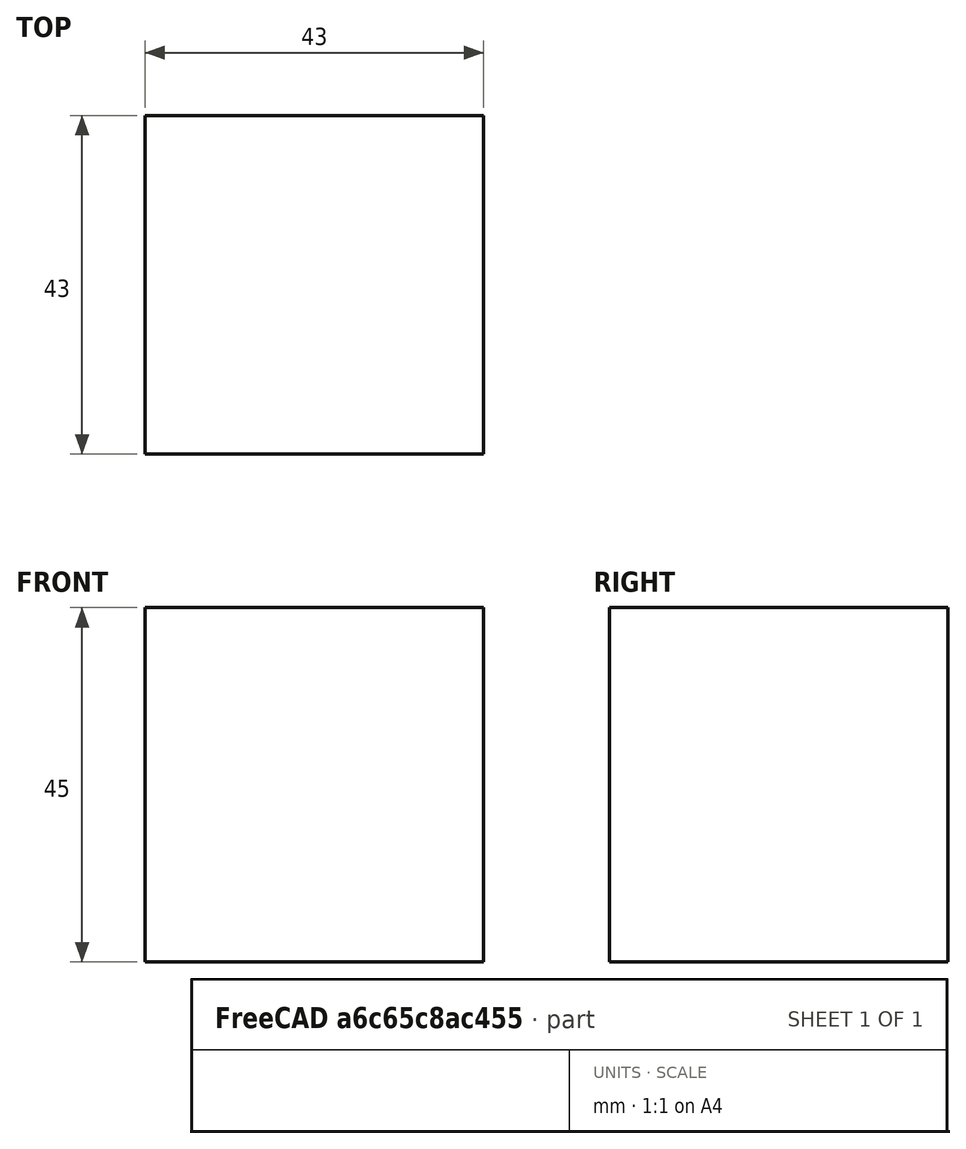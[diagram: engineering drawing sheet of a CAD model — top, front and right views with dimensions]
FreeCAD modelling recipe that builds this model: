
FCSTD DOCUMENT  (FreeCAD 0.18R16110 (Git))
Label: cadcadd
License: All rights reserved
LicenseURL: http://en.wikipedia.org/wiki/All_rights_reserved
objects: Part::Box×1, Sketcher::SketchObject×1, Part::Extrusion×1
note: 3 computed .brp shape members not serialized (recipe doc carries the construction recipe); baked Part::Feature solids carry a one-line shape summary decoded from their .brp

FEATURE [Part::Box] Box  label="Cubo"
  AttacherType = Attacher::AttachEngine3D
  Height = 45
  Length = 43
  Width = 43
FEATURE [Sketcher::SketchObject] Sketch
  MapMode = 5
  Placement = pos=(0,0,45) rot=(0,0,1;0rad)
  Support = -> [Box]
  sketch-geometry (16):
    g0: LineSegment StartX=0.982842 StartY=41.8975 StartZ=0 EndX=41.993 EndY=41.8975 EndZ=0
    g1: LineSegment StartX=0.982842 StartY=41.9957 StartZ=0 EndX=1.011 EndY=26.4994 EndZ=0
    g2: LineSegment StartX=1.011 StartY=26.4994 StartZ=0 EndX=3.72878 EndY=25.341 EndZ=0
    g3: LineSegment StartX=3.72878 StartY=25.341 StartZ=0 EndX=0.986717 EndY=25.3461 EndZ=0
    g4: LineSegment StartX=0.986717 StartY=25.3461 StartZ=0 EndX=0.986717 EndY=23.2117 EndZ=0
    g5: LineSegment StartX=0.986717 StartY=23.2117 StartZ=0 EndX=3.72852 EndY=23.2117 EndZ=0
    g6: LineSegment StartX=3.72852 StartY=23.2117 StartZ=0 EndX=0.986717 EndY=21.3736 EndZ=0
    g7: LineSegment StartX=0.986717 StartY=21.3736 StartZ=0 EndX=1.001 EndY=1 EndZ=0
    g8: LineSegment StartX=1.001 StartY=1 StartZ=0 EndX=41.9835 EndY=1 EndZ=0
    g9: LineSegment StartX=41.993 StartY=41.8975 StartZ=0 EndX=41.993 EndY=26.4994 EndZ=0
    g10: LineSegment StartX=41.993 StartY=26.4994 StartZ=0 EndX=39.4767 EndY=25.341 EndZ=0
    g11: LineSegment StartX=39.4767 StartY=25.341 StartZ=0 EndX=41.8698 EndY=25.3461 EndZ=0
    g12: LineSegment StartX=41.8698 StartY=25.3461 StartZ=0 EndX=41.8698 EndY=23.2117 EndZ=0
    g13: LineSegment StartX=41.8698 StartY=23.2117 StartZ=0 EndX=39.4785 EndY=23.2117 EndZ=0
    g14: LineSegment StartX=39.4785 StartY=23.2117 StartZ=0 EndX=41.9835 EndY=21.3736 EndZ=0
    g15: LineSegment StartX=41.9835 StartY=21.3736 StartZ=0 EndX=41.9835 EndY=1 EndZ=0
  constraints (10):
    c: Coincident(g1,g2)
    c: Coincident(g2,g3)
    c: Coincident(g3,g4)
    c: Coincident(g4,g5)
    c: Coincident(g5,g6)
    c: Coincident(g6,g7)
    c: Coincident(g10,g11)
    c: Coincident(g11,g12)
    c: Coincident(g12,g13)
    c: Coincident(g13,g14)
FEATURE [Part::Extrusion] Extrude
  Base = -> Sketch
  Dir = (0,0,1)
  DirMode = 2
  FaceMakerClass = Part::FaceMakerBullseye
  LengthFwd = 45
  LengthRev = 0
  Reversed = true
  Solid = false
  Symmetric = false
